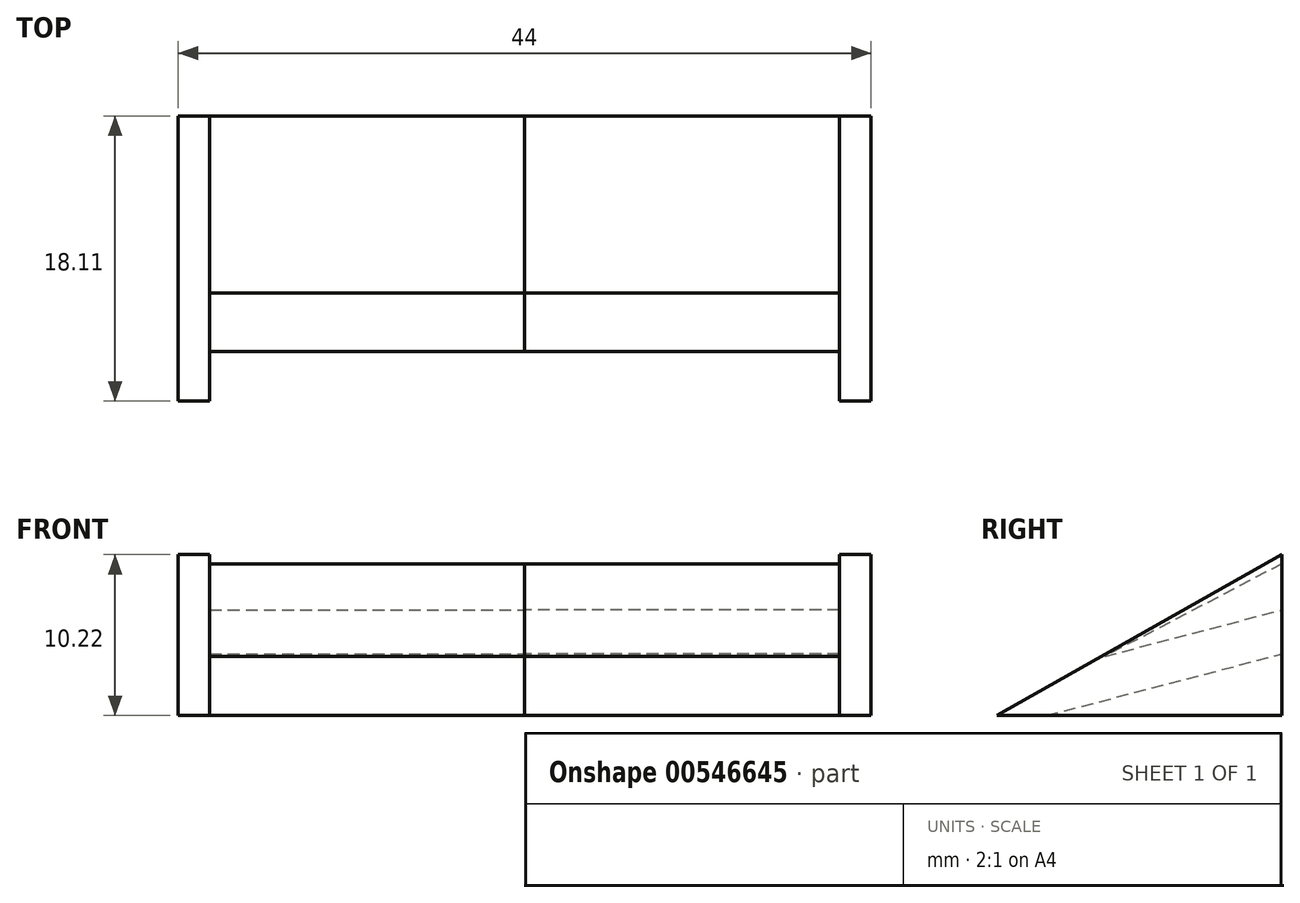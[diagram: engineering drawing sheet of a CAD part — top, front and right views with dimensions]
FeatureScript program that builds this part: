
annotation { "Feature Type Name" : "Feature", "Feature Type Description" : "" }
export const myFeature = defineFeature(function(context is Context, id is Id, definition is map)
    precondition{}
    {
        {
            var Q0;
            Q0=qCreatedBy(makeId("Right.planeOp"),FACE);
            var sketch = newSketch(context, id + "F0", { "sketchPlane" : qUnion([Q0])});
            skLineSegment(sketch, "E0", {"start": v(-85.03, -55) * mm, "end": v(-75.57, -55) * mm});
            skLineSegment(sketch, "E1.bottom", {"start": v(-85.03, -55) * mm, "end": v(-75.56, -55) * mm});
            skLineSegment(sketch, "E2", {"start": v(-75.56, -48.23) * mm, "end": v(-75.56, -48.31) * mm});
            skLineSegment(sketch, "E3", {"start": v(-75.56, -48.31) * mm, "end": v(-75.56, -48.23) * mm});
            skLineSegment(sketch, "E4", {"start": v(-81.33, -51.25) * mm, "end": v(-75.56, -48.31) * mm});
            skLineSegment(sketch, "E5", {"start": v(-85.03, -55) * mm, "end": v(-70.08, -55) * mm});
            skLineSegment(sketch, "E6", {"start": v(-70.08, -55) * mm, "end": v(-70.08, -45.37) * mm});
            skPoint(sketch, "E7.endSnap0", {"position": v(-70.08, -50.2) * mm});
            skLineSegment(sketch, "E8", {"start": v(-85.03, -55) * mm, "end": v(-70.08, -51.1) * mm});
            skLineSegment(sketch, "E9", {"start": v(-70.08, -51.1) * mm, "end": v(-70.08, -45.37) * mm});
            skLineSegment(sketch, "E10", {"start": v(-70.08, -45.37) * mm, "end": v(-81.33, -51.25) * mm});
            skLineSegment(sketch, "E11", {"start": v(-81.33, -51.25) * mm, "end": v(-70.08, -48.3) * mm});
            skPoint(sketch, "E7.end.orphan", {"position": v(-69.04, -50.2) * mm});
            skPoint(sketch, "E7.start.orphan", {"position": v(-70.08, -50.2) * mm});
            skPoint(sketch, "E12.end.orphan", {"position": v(-75.56, -45.37) * mm});
            skPoint(sketch, "E13.start.orphan", {"position": v(-80.3, -50.2) * mm});
            skLineSegment(sketch, "E14", {"start": v(-85.03, -55) * mm, "end": v(64.97, -55) * mm});
            skSolve(sketch);
        }
        {
            var Q0;
            Q0 = qSketchRegion(id + "F0", true);
            extrude(context, id + "F1", {"entities" : qUnion([Q0]), "depth" : 20 * mm, "offsetDistance" : 25 * mm});
        }
        {
            var Q0;
            Q0=makeQuery(id+"F1.opExtrude","CAP_FACE",FACE,{"disambiguationData":[OSD([sQuery(id+"F0.wireOp",EDGE,"E5"),sQuery(id+"F0.wireOp",EDGE,"E6"),sQuery(id+"F0.wireOp",EDGE,"E8")])],"isStart":false});
            var sketch = newSketch(context, id + "F2", { "sketchPlane" : qUnion([Q0])});
            skLineSegment(sketch, "E15", {"start": v(-70.08, -55) * mm, "end": v(-88.19, -55) * mm});
            skLineSegment(sketch, "E16", {"start": v(-70.08, -44.79) * mm, "end": v(-70.08, -55) * mm});
            skLineSegment(sketch, "E17", {"start": v(-88.19, -55) * mm, "end": v(-70.08, -44.79) * mm});
            skPoint(sketch, "E18.orphan", {"position": v(-70.08, -43.13) * mm});
            skSolve(sketch);
        }
        {
            var Q0;
            Q0 = qSketchRegion(id + "F2", true);
            extrude(context, id + "F3", {"entities" : qUnion([Q0]), "operationType" : NewBodyOperationType.ADD, "depth" : 2 * mm, "offsetDistance" : 25 * mm});
        }
        {
            var Q0;
            Q0=makeQuery(id+"F1.opExtrude","SWEPT_BODY",BODY,{"disambiguationData":[OSD([sQuery(id+"F0.wireOp",EDGE,"E6"),sQuery(id+"F0.wireOp",EDGE,"E8"),sQuery(id+"F0.wireOp",EDGE,"E14")])]});
            var Q1;
            Q1=makeQuery(id+"F1.opExtrude","SWEPT_BODY",BODY,{"disambiguationData":[OSD([sQuery(id+"F0.wireOp",EDGE,"E9"),sQuery(id+"F0.wireOp",EDGE,"E10"),sQuery(id+"F0.wireOp",EDGE,"E11")])]});
            var Q2;
            Q2=qCreatedBy(makeId("Right.planeOp"),FACE);
            mirror(context, id + "F4", {"entities" : qUnion([Q0, Q1]), "mirrorPlane" : qUnion([Q2])});
        }
    });
